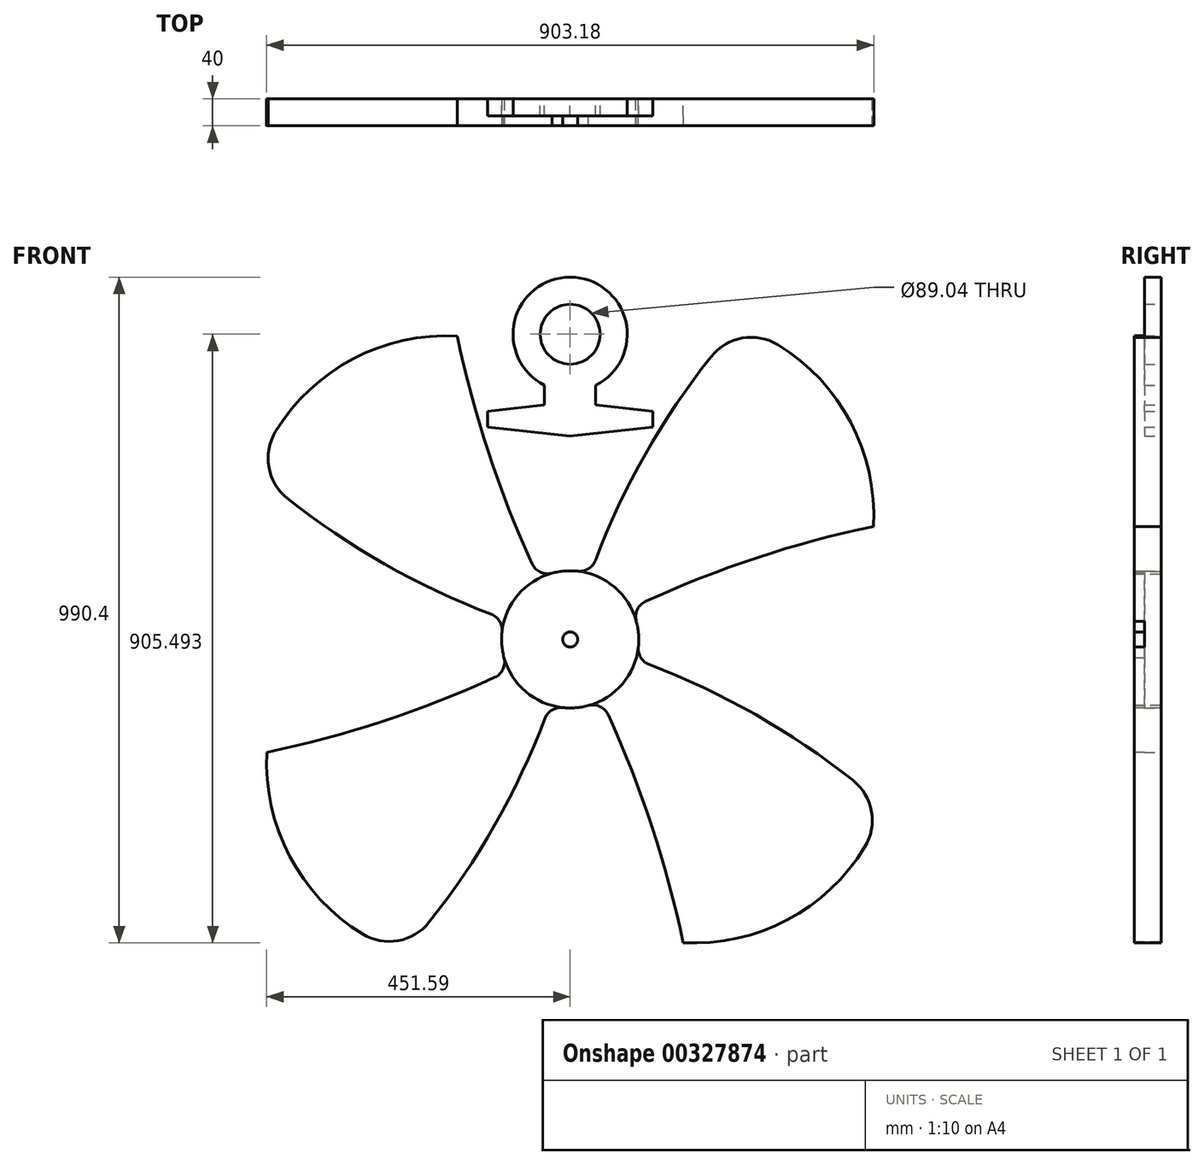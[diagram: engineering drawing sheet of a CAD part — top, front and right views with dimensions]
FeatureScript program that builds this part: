
annotation { "Feature Type Name" : "Feature", "Feature Type Description" : "" }
export const myFeature = defineFeature(function(context is Context, id is Id, definition is map)
    precondition{}
    {
        {
            var Q0;
            Q0=qCreatedBy(makeId("Front.planeOp"),FACE);
            var sketch = newSketch(context, id + "F0", { "sketchPlane" : qUnion([Q0])});
            skCircle(sketch, "E0", {"center": v(0, 439.06) * mm, "radius": 84.9 * mm});
            skLineSegment(sketch, "E1", {"start": v(-38.1, 363.18) * mm, "end": v(-38.1, 333.93) * mm});
            skLineSegment(sketch, "E2", {"start": v(38.1, 363.18) * mm, "end": v(38.1, 333.93) * mm});
            skCircle(sketch, "E3", {"center": v(0, -14.84) * mm, "radius": 102.05 * mm});
            skArc(sketch, "E4", {"start": v(-168.06, 436.32) * mm, "mid": v(-322.67, 402.5) * mm, "end": v(-438.15, 294.27) * mm});
            skArc(sketch, "E5", {"start": v(-420.5, 194.8) * mm, "mid": v(-275.7, 97.1) * mm, "end": v(-117.67, 22.7) * mm});
            skArc(sketch, "E6", {"start": v(-168.06, 436.32) * mm, "mid": v(-121.72, 263.87) * mm, "end": v(-56.67, 97.56) * mm});
            skArc(sketch, "E7", {"start": v(-438.15, 294.27) * mm, "mid": v(-448.17, 241.19) * mm, "end": v(-420.5, 194.8) * mm});
            skArc(sketch, "E8", {"start": v(-451.17, -182.9) * mm, "mid": v(-417.34, -337.51) * mm, "end": v(-309.1, -453) * mm});
            skArc(sketch, "E9", {"start": v(-209.64, -435.34) * mm, "mid": v(-111.94, -290.55) * mm, "end": v(-37.54, -132.52) * mm});
            skArc(sketch, "E10", {"start": v(-451.17, -182.9) * mm, "mid": v(-278.7, -136.57) * mm, "end": v(-112.4, -71.51) * mm});
            skArc(sketch, "E11", {"start": v(-309.1, -453) * mm, "mid": v(-256.03, -463.02) * mm, "end": v(-209.64, -435.34) * mm});
            skArc(sketch, "E12", {"start": v(168.06, -466) * mm, "mid": v(322.67, -432.18) * mm, "end": v(438.15, -323.95) * mm});
            skArc(sketch, "E13", {"start": v(420.5, -224.48) * mm, "mid": v(275.7, -126.78) * mm, "end": v(117.67, -52.38) * mm});
            skArc(sketch, "E14", {"start": v(168.06, -466) * mm, "mid": v(121.72, -293.55) * mm, "end": v(56.67, -127.25) * mm});
            skArc(sketch, "E15", {"start": v(438.15, -323.95) * mm, "mid": v(448.17, -270.87) * mm, "end": v(420.5, -224.48) * mm});
            skArc(sketch, "E16", {"start": v(451.17, 153.22) * mm, "mid": v(417.34, 307.83) * mm, "end": v(309.1, 423.3) * mm});
            skArc(sketch, "E17", {"start": v(209.64, 405.65) * mm, "mid": v(111.94, 260.87) * mm, "end": v(37.54, 102.83) * mm});
            skArc(sketch, "E18", {"start": v(451.17, 153.22) * mm, "mid": v(278.7, 106.88) * mm, "end": v(112.4, 41.83) * mm});
            skArc(sketch, "E19", {"start": v(309.1, 423.3) * mm, "mid": v(256.03, 433.33) * mm, "end": v(209.64, 405.65) * mm});
            skArc(sketch, "E20", {"start": v(-101.45, -3.8) * mm, "mid": v(-105.04, 12.22) * mm, "end": v(-117.67, 22.7) * mm});
            skArc(sketch, "E21", {"start": v(-56.67, 97.56) * mm, "mid": v(-44.34, 85.1) * mm, "end": v(-26.87, 83.6) * mm});
            skArc(sketch, "E22", {"start": v(-112.4, -71.51) * mm, "mid": v(-99.95, -59.18) * mm, "end": v(-98.44, -41.72) * mm});
            skArc(sketch, "E23", {"start": v(-11.05, -116.29) * mm, "mid": v(-27.07, -119.88) * mm, "end": v(-37.54, -132.52) * mm});
            skArc(sketch, "E24", {"start": v(56.67, -127.25) * mm, "mid": v(44.34, -114.79) * mm, "end": v(26.87, -113.29) * mm});
            skArc(sketch, "E25", {"start": v(101.45, -25.9) * mm, "mid": v(105.04, -41.9) * mm, "end": v(117.67, -52.38) * mm});
            skArc(sketch, "E26", {"start": v(112.4, 41.83) * mm, "mid": v(99.95, 29.5) * mm, "end": v(98.44, 12.03) * mm});
            skArc(sketch, "E27", {"start": v(11.05, 86.6) * mm, "mid": v(27.07, 90.2) * mm, "end": v(37.54, 102.83) * mm});
            skArc(sketch, "E28", {"start": v(405.87, -97.68) * mm, "mid": v(455.8, 0.63) * mm, "end": v(483.94, 107.25) * mm});
            skArc(sketch, "E29", {"start": v(546.67, -113.68) * mm, "mid": v(542.56, 4.52) * mm, "end": v(483.94, 107.25) * mm});
            skEllipticalArc(sketch, "E30", {});
            skEllipticalArc(sketch, "E31", {});
            skArc(sketch, "E32", {"start": v(546.67, -113.68) * mm, "mid": v(532.07, -90.07) * mm, "end": v(514.7, -68.4) * mm});
            skArc(sketch, "E33", {"start": v(461.42, -68.4) * mm, "mid": v(433.29, -82.36) * mm, "end": v(405.87, -97.68) * mm});
            skArc(sketch, "E34", {"start": v(-483.94, 107.25) * mm, "mid": v(-455.8, 0.63) * mm, "end": v(-405.87, -97.68) * mm});
            skArc(sketch, "E35", {"start": v(-483.94, 107.25) * mm, "mid": v(-542.56, 4.52) * mm, "end": v(-546.67, -113.68) * mm});
            skArc(sketch, "E36", {"start": v(-514.7, -68.4) * mm, "mid": v(-532.07, -90.07) * mm, "end": v(-546.67, -113.68) * mm});
            skArc(sketch, "E37", {"start": v(-405.87, -97.68) * mm, "mid": v(-433.29, -82.36) * mm, "end": v(-461.42, -68.4) * mm});
            skArc(sketch, "E38", {"start": v(0, -523.97) * mm, "mid": v(-27.79, -480.97) * mm, "end": v(-72.9, -456.75) * mm});
            skArc(sketch, "E39", {"start": v(72.9, -456.75) * mm, "mid": v(27.79, -480.97) * mm, "end": v(0, -523.97) * mm});
            skEllipticalArc(sketch, "E40", {});
            skEllipticalArc(sketch, "E41", {});
            skArc(sketch, "E42", {"start": v(38.1, -247.36) * mm, "mid": v(62, -297.08) * mm, "end": v(113.73, -316.3) * mm});
            skArc(sketch, "E43", {"start": v(-113.73, -316.3) * mm, "mid": v(-62, -297.08) * mm, "end": v(-38.1, -247.36) * mm});
            skLineSegment(sketch, "E44", {"start": v(-122.73, 324.63) * mm, "end": v(0, 338.12) * mm});
            skLineSegment(sketch, "E45", {"start": v(-122.73, 324.63) * mm, "end": v(-122.73, 300.77) * mm});
            skLineSegment(sketch, "E46", {"start": v(-122.73, 300.77) * mm, "end": v(0, 287.28) * mm});
            skLineSegment(sketch, "E47", {"start": v(122.73, 324.63) * mm, "end": v(0, 338.12) * mm});
            skLineSegment(sketch, "E48", {"start": v(122.73, 324.63) * mm, "end": v(122.73, 300.77) * mm});
            skLineSegment(sketch, "E49", {"start": v(122.73, 300.77) * mm, "end": v(0, 287.28) * mm});
            skCircle(sketch, "E50", {"center": v(0, -14.84) * mm, "radius": 11.25 * mm});
            skEllipticalArc(sketch, "E51", {});
            skEllipticalArc(sketch, "E52", {});
            skEllipticalArc(sketch, "E53", {});
            skEllipticalArc(sketch, "E54", {});
            skLineSegment(sketch, "E55", {"start": v(38.1, 291.47) * mm, "end": v(38.1, 104.3) * mm});
            skLineSegment(sketch, "E56", {"start": v(-38.1, 291.47) * mm, "end": v(-38.1, 83.11) * mm});
            skLineSegment(sketch, "E57", {"start": v(-38.1, -133.98) * mm, "end": v(-38.1, -247.36) * mm});
            skLineSegment(sketch, "E58", {"start": v(38.1, -112.8) * mm, "end": v(38.1, -247.36) * mm});
            skCircle(sketch, "E59", {"center": v(0, 439.06) * mm, "radius": 44.52 * mm});
            const initialGuessF0  = {"E30": [0, -0.0684062639999998, -18.166049, 0, 0.46141764460000007, 0.25577825400000004, 0, 0.43309], "E31": [0, -0.0684062639999998, -20.263785, 0, 0.514700139, 0.39229769140000004, 0, 0.531867], "E40": [0, -0.0684062639999998, -20.263785, 0, 0.514700139, 0.39229769140000004, 1.712903, 1.892029], "E41": [0, -0.0684062639999998, -18.166049, 0, 0.46141764460000007, 0.25577825400000004, 1.819833, 1.852627], "E51": [0, -0.0684062639999998, -18.166049, 0, 0.46141764460000007, 0.25577825400000004, 1.29439, 1.32176], "E52": [0, -0.0684062639999998, -20.263785, 0, 0.514700139, 0.39229769140000004, 1.162721, 1.42869], "E53": [0, -0.0684062639999998, -20.263785, 0, 0.514700139, 0.39229769140000004, 2.62094, 3.141593], "E54": [0, -0.0684062639999998, -18.166049, 0, 0.46141764460000007, 0.25577825400000004, 2.587742, 3.141593]};
            skSetInitialGuess(sketch, initialGuessF0);
            skSolve(sketch);
        }
        {
            var Q0;
            Q0 = qSketchRegion(id + "F0", true);
            extrude(context, id + "F1", {"entities" : qUnion([Q0]), "depth" : 25 * mm});
        }
        {
            var Q0;
            {var subQ0=sQuery(id+"F0.wireOp",EDGE,"E11");Q0=makeQuery(id+"F0.imprint","IMPRINT",FACE,{"disambiguationData":[TD([[makeQuery(id+"F0.imprint","IMPRINT",EDGE,{"derivedFrom":subQ0}),1.0]])]});}
            var Q1;
            Q1=makeQuery(id+"F0.imprint","IMPRINT",FACE,{"disambiguationData":[TD([[makeQuery(id+"F0.imprint","IMPRINT",EDGE,{"derivedFrom":sQuery(id+"F0.wireOp",EDGE,"E4")}),1.0]])]});
            var Q2;
            {var subQ8=sQuery(id+"F0.wireOp",EDGE,"E12");Q2=makeQuery(id+"F0.imprint","IMPRINT",FACE,{"disambiguationData":[TD([[makeQuery(id+"F0.imprint","IMPRINT",EDGE,{"derivedFrom":subQ8}),1.0]])]});}
            var Q3;
            Q3=makeQuery(id+"F0.imprint","IMPRINT",FACE,{"disambiguationData":[TD([[makeQuery(id+"F0.imprint","IMPRINT",EDGE,{"derivedFrom":sQuery(id+"F0.wireOp",EDGE,"E16")}),1.0]])]});
            var Q4;
            Q4=makeQuery(id+"F0.imprint","IMPRINT",FACE,{"disambiguationData":[TD([[makeQuery(id+"F0.imprint","IMPRINT",EDGE,{"derivedFrom":sQuery(id+"F0.wireOp",EDGE,"E50")}),1.0]])]});
            extrude(context, id + "F2", {"entities" : qUnion([Q0, Q1, Q2, Q3, Q4]), "operationType" : NewBodyOperationType.ADD, "depth" : 40 * mm});
        }
    });
